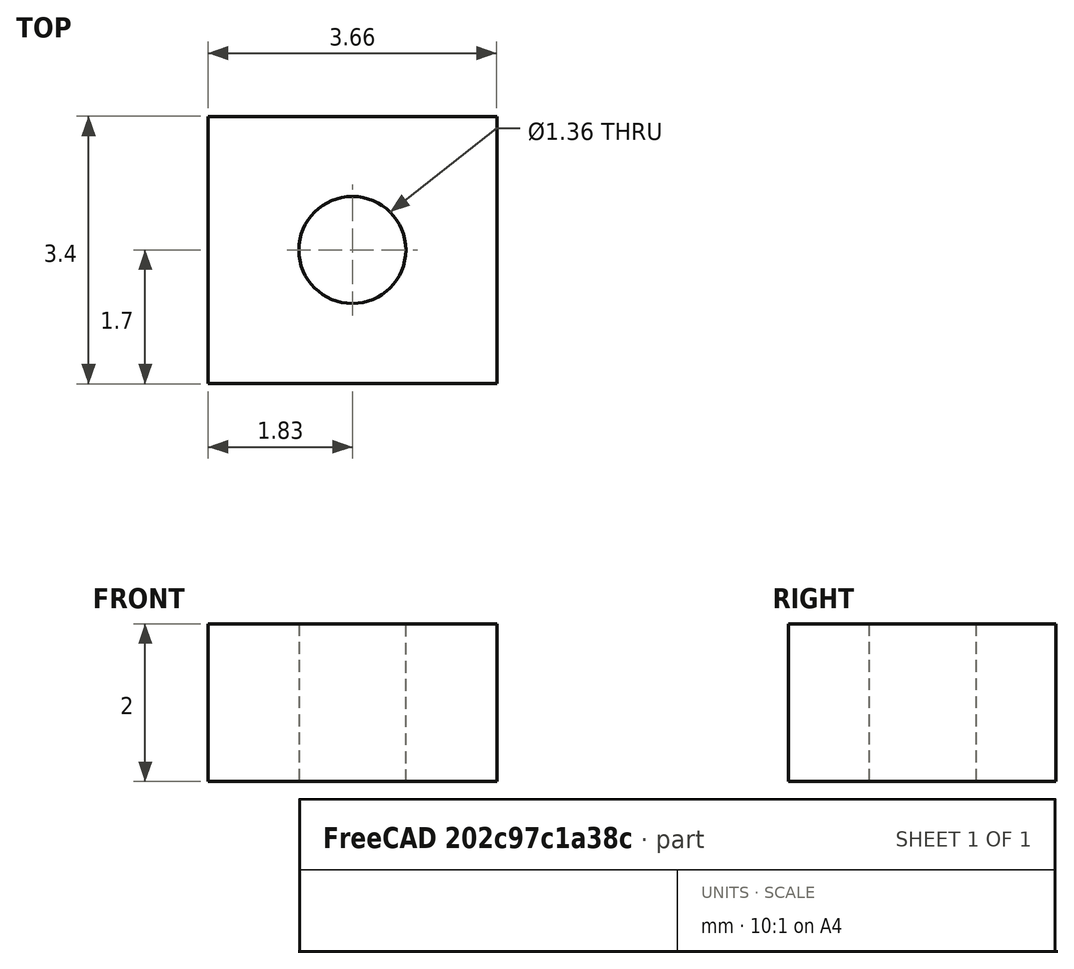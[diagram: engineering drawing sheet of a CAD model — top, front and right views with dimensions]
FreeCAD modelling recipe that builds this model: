
FCSTD DOCUMENT  (FreeCAD 0.20R29603 (Git))
Label: Pistão
License: All rights reserved
LicenseURL: http://en.wikipedia.org/wiki/All_rights_reserved
objects: Sketcher::SketchObject×1, PartDesign::Pad×1, PartDesign::Body×1
note: 4 computed .brp shape members not serialized (recipe doc carries the construction recipe); baked Part::Feature solids carry a one-line shape summary decoded from their .brp

FEATURE [Sketcher::SketchObject] Sketch
  FullyConstrained = false
  MapMode = 5
  Support = -> [XY_Plane]
  sketch-geometry (6):
    g0: LineSegment StartX=-1.835 StartY=1.69787 StartZ=0 EndX=-1.835 EndY=-1.69787 EndZ=0
    g1: LineSegment StartX=-1.835 StartY=-1.69787 StartZ=0 EndX=1.835 EndY=-1.69787 EndZ=0
    g2: LineSegment StartX=1.835 StartY=-1.69787 StartZ=0 EndX=1.835 EndY=1.69787 EndZ=0
    g3: LineSegment StartX=1.835 StartY=1.69787 StartZ=0 EndX=-1.835 EndY=1.69787 EndZ=0
    g4: GeomPoint X=0 Y=0 Z=0
    g5: Circle CenterX=0 CenterY=0 CenterZ=0 NormalX=0 NormalY=0 NormalZ=1 AngleXU=0 Radius=0.679783
  constraints (13):
    c: Coincident(g0,g1)
    c: Coincident(g1,g2)
    c: Coincident(g2,g3)
    c: Coincident(g3,g0)
    c: Horizontal(g1)
    c: Horizontal(g3)
    c: Vertical(g0)
    c: Vertical(g2)
    c: Symmetric(g1,g0,g4)
    c: Coincident(g4,g-1)
    c: Coincident(g5,g4)
    c: Distance(g0,g2) = 5
    c: Distance(g3) = 3.67
FEATURE [PartDesign::Pad] Pad
  Direction = (0,0,1)
  Length = 2
  Length2 = 10
  Profile = -> Sketch
  ReferenceAxis = -> Sketch [N_Axis]
  Refine = true
  Type = 0
FEATURE [PartDesign::Body] Body
  Group = -> [Sketch,Pad]
  Origin = -> Origin
  Tip = -> Pad
